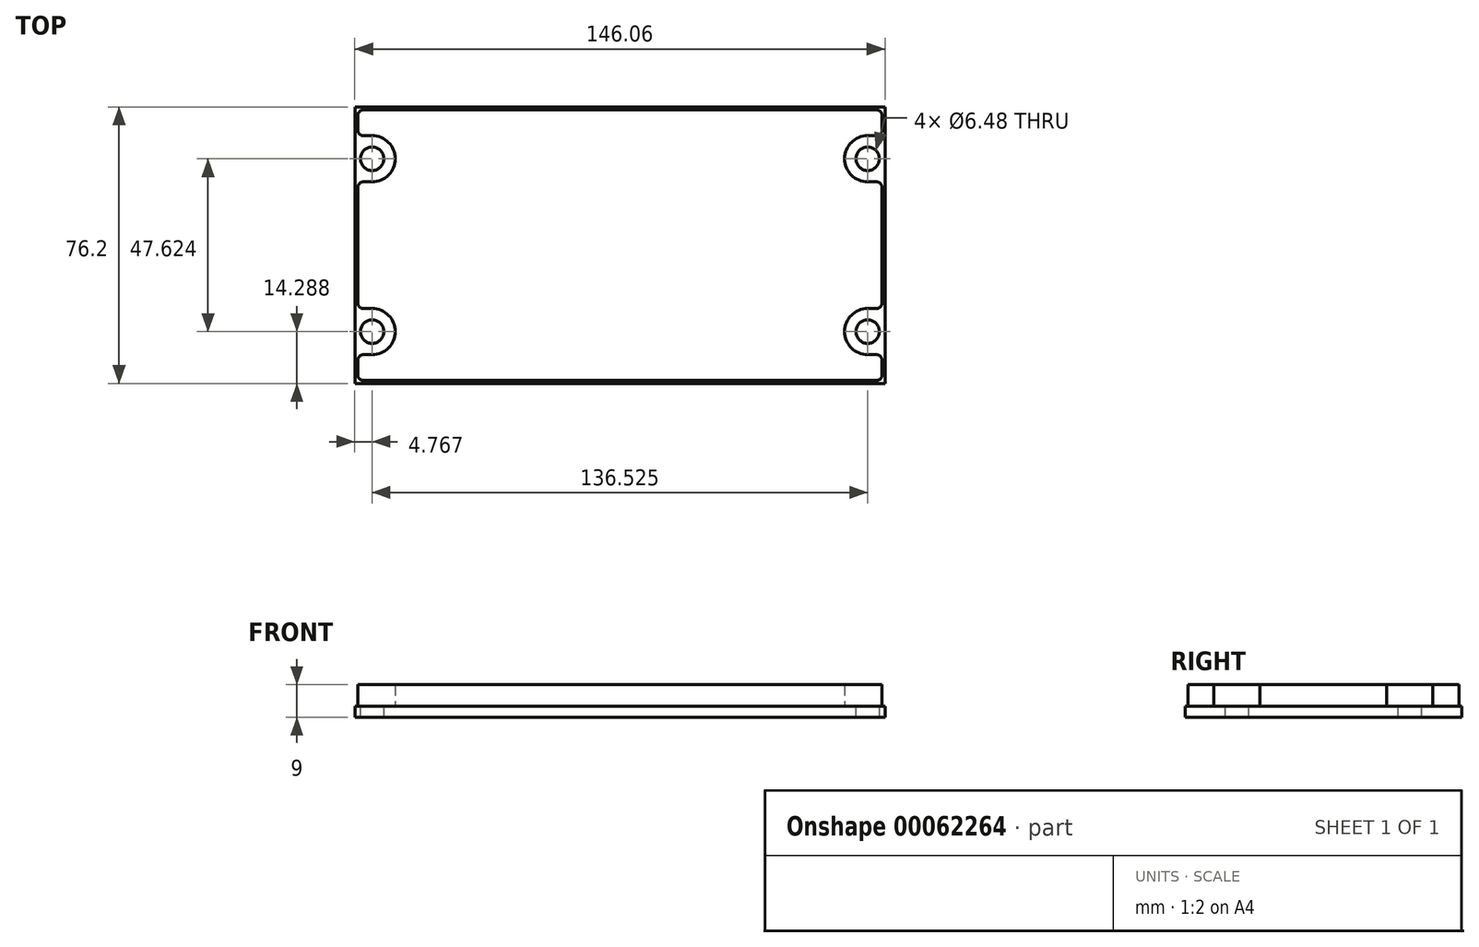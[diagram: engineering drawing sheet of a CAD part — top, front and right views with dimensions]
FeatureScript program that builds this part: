
annotation { "Feature Type Name" : "Feature", "Feature Type Description" : "" }
export const myFeature = defineFeature(function(context is Context, id is Id, definition is map)
    precondition{}
    {
        {
            var Q0;
            Q0=qCreatedBy(makeId("Top.planeOp"),FACE);
            var sketch = newSketch(context, id + "F0", { "sketchPlane" : qUnion([Q0])});
            skLineSegment(sketch, "E0.bottom", {"start": v(73.03, 38.1) * mm, "end": v(-73.02, 38.1) * mm});
            skLineSegment(sketch, "E0.top", {"start": v(73.03, -38.1) * mm, "end": v(-73.02, -38.1) * mm});
            skLineSegment(sketch, "E0.left", {"start": v(73.02, 38.1) * mm, "end": v(73.03, -38.1) * mm});
            skLineSegment(sketch, "E0.right", {"start": v(-73.03, 38.1) * mm, "end": v(-73.02, -38.1) * mm});
            skPoint(sketch, "E0.middle", {"position": v(0, 0) * mm});
            skLineSegment(sketch, "E1.bottom", {"start": v(-72.22, 37.3) * mm, "end": v(72.22, 37.3) * mm});
            skLineSegment(sketch, "E1.top", {"start": v(-72.22, -37.3) * mm, "end": v(72.22, -37.3) * mm});
            skLineSegment(sketch, "E1.left", {"start": v(-72.22, 37.3) * mm, "end": v(-72.22, 30.16) * mm});
            skLineSegment(sketch, "E1.right", {"start": v(72.22, 37.3) * mm, "end": v(72.22, 30.16) * mm});
            skCircle(sketch, "E2", {"center": v(-68.26, 23.81) * mm, "radius": 3.24 * mm});
            skLineSegment(sketch, "E3", {"start": v(-68.26, 30.16) * mm, "end": v(-72.22, 30.16) * mm});
            skLineSegment(sketch, "E4", {"start": v(-68.26, 17.46) * mm, "end": v(-72.22, 17.46) * mm});
            skLineSegment(sketch, "E5.trimOffspring", {"start": v(-72.22, 17.46) * mm, "end": v(-72.22, -17.46) * mm});
            skArc(sketch, "E6.trimOffspring", {"start": v(-68.26, 17.46) * mm, "mid": v(-61.91, 23.81) * mm, "end": v(-68.26, 30.16) * mm});
            skLineSegment(sketch, "E7.MirrorCS", {"start": v(68.26, 17.46) * mm, "end": v(72.22, 17.46) * mm});
            skArc(sketch, "E8.MirrorCS", {"start": v(68.26, 17.46) * mm, "mid": v(61.91, 23.81) * mm, "end": v(68.26, 30.16) * mm});
            skCircle(sketch, "E9.MirrorC", {"center": v(68.26, 23.81) * mm, "radius": 3.24 * mm});
            skLineSegment(sketch, "E10.MirrorCS", {"start": v(68.26, 30.16) * mm, "end": v(72.22, 30.16) * mm});
            skLineSegment(sketch, "E11.MirrorCS", {"start": v(-68.26, -30.16) * mm, "end": v(-72.22, -30.16) * mm});
            skCircle(sketch, "E12.MirrorC", {"center": v(-68.26, -23.81) * mm, "radius": 3.24 * mm});
            skLineSegment(sketch, "E13.MirrorCS", {"start": v(-68.26, -17.46) * mm, "end": v(-72.22, -17.46) * mm});
            skArc(sketch, "E14.MirrorCS", {"start": v(-68.26, -17.46) * mm, "mid": v(-61.91, -23.81) * mm, "end": v(-68.26, -30.16) * mm});
            skArc(sketch, "E15.MirrorCS", {"start": v(68.26, -17.46) * mm, "mid": v(61.91, -23.81) * mm, "end": v(68.26, -30.16) * mm});
            skCircle(sketch, "E16.MirrorC", {"center": v(68.26, -23.81) * mm, "radius": 3.24 * mm});
            skLineSegment(sketch, "E17.MirrorCS", {"start": v(68.26, -30.16) * mm, "end": v(72.22, -30.16) * mm});
            skLineSegment(sketch, "E18.MirrorCS", {"start": v(68.26, -17.46) * mm, "end": v(72.22, -17.46) * mm});
            skLineSegment(sketch, "E19.trimOffspring", {"start": v(72.22, 17.46) * mm, "end": v(72.22, -17.46) * mm});
            skLineSegment(sketch, "E20.trimOffspring", {"start": v(72.22, -30.16) * mm, "end": v(72.22, -37.3) * mm});
            skLineSegment(sketch, "E21.trimOffspring", {"start": v(-72.22, -30.16) * mm, "end": v(-72.22, -37.3) * mm});
            skSolve(sketch);
        }
        {
            var Q0;
            Q0=makeQuery(id+"F0.imprint","IMPRINT",FACE,{"disambiguationData":[TD([[makeQuery(id+"F0.imprint","IMPRINT",EDGE,{"derivedFrom":sQuery(id+"F0.wireOp",EDGE,"E0.bottom")}),1.0]])]});
            var Q1;
            Q1=makeQuery(id+"F0.imprint","IMPRINT",FACE,{"disambiguationData":[TD([[makeQuery(id+"F0.imprint","IMPRINT",EDGE,{"derivedFrom":sQuery(id+"F0.wireOp",EDGE,"E1.bottom")}),-1.0]])]});
            extrude(context, id + "F1", {"entities" : qUnion([Q0, Q1]), "oppositeDirection" : true, "depth" : 3 * mm, "offsetDistance" : 25 * mm});
        }
        {
            var Q0;
            Q0=makeQuery(id+"F0.imprint","IMPRINT",FACE,{"disambiguationData":[TD([[makeQuery(id+"F0.imprint","IMPRINT",EDGE,{"derivedFrom":sQuery(id+"F0.wireOp",EDGE,"E1.bottom")}),-1.0]])]});
            extrude(context, id + "F2", {"entities" : qUnion([Q0]), "depth" : 6 * mm, "offsetDistance" : 25 * mm});
        }
        {
            var Q0;
            Q0=makeQuery(id+"F2.opExtrude","SWEPT_EDGE",EDGE,{"disambiguationData":[OSD([sQuery(id+"F0.wireOp",EDGE,"E1.bottom"),sQuery(id+"F0.wireOp",EDGE,"E1.left")])]});
            var Q1;
            Q1=makeQuery(id+"F2.opExtrude","SWEPT_EDGE",EDGE,{"disambiguationData":[OSD([sQuery(id+"F0.wireOp",EDGE,"E1.left"),sQuery(id+"F0.wireOp",EDGE,"E3")])]});
            var Q2;
            Q2=makeQuery(id+"F2.opExtrude","SWEPT_EDGE",EDGE,{"disambiguationData":[OSD([sQuery(id+"F0.wireOp",EDGE,"E4"),sQuery(id+"F0.wireOp",EDGE,"E5.trimOffspring")])]});
            var Q3;
            Q3=makeQuery(id+"F2.opExtrude","SWEPT_EDGE",EDGE,{"disambiguationData":[OSD([sQuery(id+"F0.wireOp",EDGE,"E5.trimOffspring"),sQuery(id+"F0.wireOp",EDGE,"E13.MirrorCS")])]});
            var Q4;
            Q4=makeQuery(id+"F2.opExtrude","SWEPT_EDGE",EDGE,{"disambiguationData":[OSD([sQuery(id+"F0.wireOp",EDGE,"E11.MirrorCS"),sQuery(id+"F0.wireOp",EDGE,"E21.trimOffspring")])]});
            var Q5;
            Q5=makeQuery(id+"F2.opExtrude","SWEPT_EDGE",EDGE,{"disambiguationData":[OSD([sQuery(id+"F0.wireOp",EDGE,"E1.top"),sQuery(id+"F0.wireOp",EDGE,"E21.trimOffspring")])]});
            var Q6;
            Q6=makeQuery(id+"F2.opExtrude","SWEPT_EDGE",EDGE,{"disambiguationData":[OSD([sQuery(id+"F0.wireOp",EDGE,"E1.bottom"),sQuery(id+"F0.wireOp",EDGE,"E1.right")])]});
            var Q7;
            Q7=makeQuery(id+"F2.opExtrude","SWEPT_EDGE",EDGE,{"disambiguationData":[OSD([sQuery(id+"F0.wireOp",EDGE,"E1.right"),sQuery(id+"F0.wireOp",EDGE,"E10.MirrorCS")])]});
            var Q8;
            Q8=makeQuery(id+"F2.opExtrude","SWEPT_EDGE",EDGE,{"disambiguationData":[OSD([sQuery(id+"F0.wireOp",EDGE,"E7.MirrorCS"),sQuery(id+"F0.wireOp",EDGE,"E19.trimOffspring")])]});
            var Q9;
            Q9=makeQuery(id+"F2.opExtrude","SWEPT_EDGE",EDGE,{"disambiguationData":[OSD([sQuery(id+"F0.wireOp",EDGE,"E18.MirrorCS"),sQuery(id+"F0.wireOp",EDGE,"E19.trimOffspring")])]});
            var Q10;
            Q10=makeQuery(id+"F2.opExtrude","SWEPT_EDGE",EDGE,{"disambiguationData":[OSD([sQuery(id+"F0.wireOp",EDGE,"E17.MirrorCS"),sQuery(id+"F0.wireOp",EDGE,"E20.trimOffspring")])]});
            var Q11;
            Q11=makeQuery(id+"F2.opExtrude","SWEPT_EDGE",EDGE,{"disambiguationData":[OSD([sQuery(id+"F0.wireOp",EDGE,"E1.top"),sQuery(id+"F0.wireOp",EDGE,"E20.trimOffspring")])]});
            fillet(context, id + "F3", {"entities" : qUnion([Q0, Q1, Q2, Q3, Q4, Q5, Q6, Q7, Q8, Q9, Q10, Q11]), "radius" : 1.59 * mm, "tangentPropagation" : true, "allowEdgeOverflow" : false});
        }
    });
